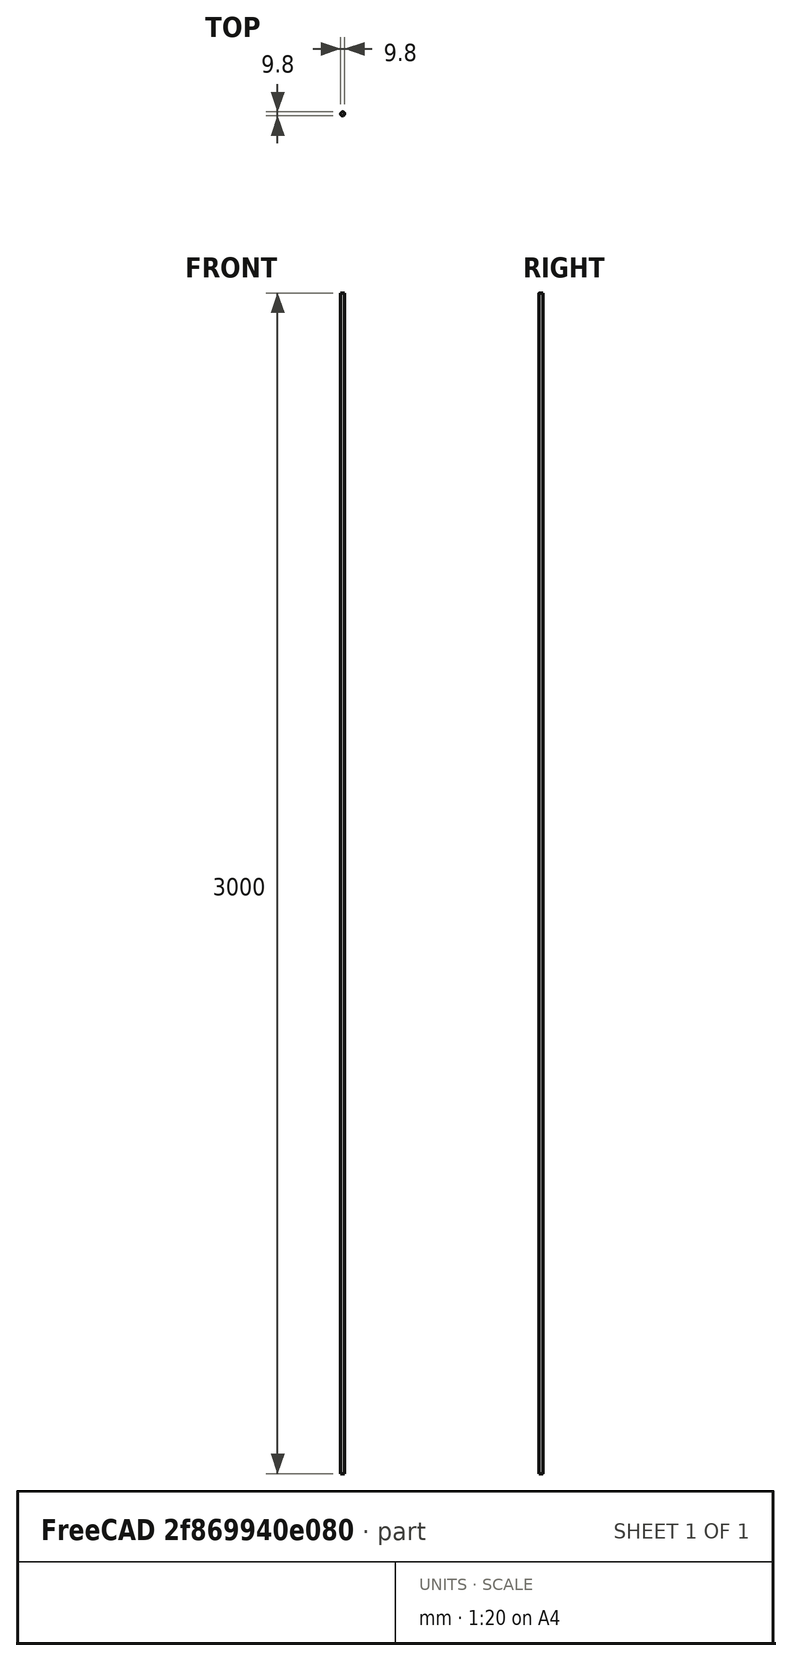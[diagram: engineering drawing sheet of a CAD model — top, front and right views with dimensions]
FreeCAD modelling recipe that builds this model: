
FCSTD DOCUMENT  (FreeCAD 0.21R33771 (Git))
Label: longFuelLowRes
License: All rights reserved
LicenseURL: http://en.wikipedia.org/wiki/All_rights_reserved
objects: Part::FeaturePython×5, App::DocumentObjectGroupPython×2, Sketcher::SketchObject×1, PartDesign::Pad×1, PartDesign::Body×1, App::MaterialObjectPython×1, Fem::FemMeshObject×1
note: 9 computed .brp shape members not serialized (recipe doc carries the construction recipe); baked Part::Feature solids carry a one-line shape summary decoded from their .brp

FEATURE [Sketcher::SketchObject] Sketch
  FullyConstrained = true
  MapMode = 5
  Support = -> [XY_Plane]
  sketch-geometry (1):
    g0: Circle CenterX=0 CenterY=0 CenterZ=0 NormalX=0 NormalY=0 NormalZ=1 AngleXU=0 Radius=4.9
  constraints (2):
    c: Coincident(g0,g-1)
    c: Diameter(g0) = 9.8
FEATURE [PartDesign::Pad] Pad
  Direction = (0,0,1)
  Length = 3000
  Length2 = 10
  Profile = -> Sketch
  ReferenceAxis = -> Sketch [N_Axis]
  Type = 0
FEATURE [PartDesign::Body] Body
  Group = -> [Sketch,Pad]
  Origin = -> Origin
  Tip = -> Pad
FEATURE [Part::FeaturePython] PhysicsModel  # WARN: FeaturePython — macro-defined, semantics opaque (R4)
  Flow = 1
  Phase = 0
  SRFModelAxis = (0,0,0)
  SRFModelCoR = (0,0,0)
  SRFModelEnabled = false
  SRFModelRPM = 0
  Time = 0
  Turbulence = 1
  TurbulenceModel = 0
  gx = 0
  gy = 0
  gz = -9800
FEATURE [App::MaterialObjectPython] FluidProperties  label="Air"  # material (typed FeaturePython)
  Category = 1
  Material = CardName=AirCompressible; Cp=1004.703 J/kg/K; Description=Compressible air properties; MolarMass=0.0289643897748887 kg/mol; Name=Air; SutherlandRefTemperature=273.15 K; SutherlandRefViscosity=1.716e-5 kg/m/s; SutherlandTemperature=110.4 K; Type=Compressible
FEATURE [Part::FeaturePython] InitialiseFields  # WARN: FeaturePython — macro-defined, semantics opaque (R4)
  PotentialFlow = false
  PotentialFlowP = false
  Pressure = 100
  ReThetat = 1
  Temperature = 800
  UseInletTemperatureValue = false
  UseInletTurbulenceValues = false
  UseInletUValues = false
  UseOutletPValue = false
  Ux = 0
  Uy = 0
  Uz = 0
  epsilon = 50000000
  gammaInt = 1
  k = 10000
  nuTilda = 55000000
  nut = 50000000
  omega = 1
FEATURE [Part::FeaturePython] CfdSolver  # WARN: FeaturePython — macro-defined, semantics opaque (R4)
  ConvergenceTol = 0.001
  EndTime = 1
  InputCaseName = case
  MaxCFLNumber = 5
  MaxInterfaceCFLNumber = 5
  MaxIterations = 2000
  Parallel = true
  ParallelCores = 4
  PurgeWrite = 0
  StartFrom = 0
  SteadyWriteInterval = 100
  TimeStep = 0.001
  TransientWriteInterval = 0.1
FEATURE [Part::FeaturePython] CfdFluidBoundary001  label="endCaps"  # WARN: FeaturePython — macro-defined, semantics opaque (R4)
  BoundarySubType = 0
  BoundaryType = 0
  DefaultBoundary = false
  DissipationRate = 50000000
  HeatFlux = 0
  HeatTransferCoeff = 0
  Intermittency = 1
  MassFlowRate = 0
  NuTilda = 55000000
  PeriodicCentreOfRotation = (0,0,0)
  PeriodicCentreOfRotationAxis = (0,0,0)
  PeriodicMaster = true
  PeriodicSeparationVector = (0,0,0)
  PorousBaffleMethod = 0
  Pressure = 100
  PressureDropCoeff = 0
  ReThetat = 1
  RelativeToFrame = false
  ReverseNormal = false
  RotationalPeriodic = false
  RoughnessConstant = 0.5
  RoughnessHeight = 0
  ScreenSpacing = 2
  ScreenWireDiameter = 0.2
  ShapeRefs = -> [Pad]
  SlipRatio = 0
  SpecificDissipationRate = 1
  Temperature = 290
  ThermalBoundaryType = 1
  TurbulenceInletSpecification = 6
  TurbulenceIntensityPercentage = 1
  TurbulenceLengthScale = 100
  TurbulentKineticEnergy = 10000
  TurbulentViscosity = 50000000
  Ux = 0
  Uy = 0
  Uz = 0
  VelocityIsCartesian = true
  VelocityMag = 0
  VolFlowRate = 0
  kEqnTurbulentKineticEnergy = 10000
  kEqnTurbulentViscosity = 50000000
FEATURE [Part::FeaturePython] CfdFluidBoundary  label="circularWall"  # WARN: FeaturePython — macro-defined, semantics opaque (R4)
  BoundarySubType = 0
  BoundaryType = 0
  DefaultBoundary = false
  DissipationRate = 50000000
  HeatFlux = 220000
  HeatTransferCoeff = 0
  Intermittency = 1
  MassFlowRate = 0
  NuTilda = 55000000
  PeriodicCentreOfRotation = (0,0,0)
  PeriodicCentreOfRotationAxis = (0,0,0)
  PeriodicMaster = true
  PeriodicSeparationVector = (0,0,0)
  PorousBaffleMethod = 0
  Pressure = 100
  PressureDropCoeff = 0
  ReThetat = 1
  RelativeToFrame = false
  ReverseNormal = false
  RotationalPeriodic = false
  RoughnessConstant = 0.5
  RoughnessHeight = 0
  ScreenSpacing = 2
  ScreenWireDiameter = 0.2
  ShapeRefs = -> [Pad]
  SlipRatio = 0
  SpecificDissipationRate = 1
  Temperature = 290
  ThermalBoundaryType = 2
  TurbulenceInletSpecification = 6
  TurbulenceIntensityPercentage = 1
  TurbulenceLengthScale = 100
  TurbulentKineticEnergy = 10000
  TurbulentViscosity = 50000000
  Ux = 0
  Uy = 0
  Uz = 0
  VelocityIsCartesian = true
  VelocityMag = 0
  VolFlowRate = 0
  kEqnTurbulentKineticEnergy = 10000
  kEqnTurbulentViscosity = 50000000
FEATURE [Fem::FemMeshObject] Pad_MeshSurfaceMesh
FEATURE [App::DocumentObjectGroupPython] Pad_Mesh  # scripted group (container) (typed FeaturePython)
  CaseName = meshCase
  CellsBetweenLevels = 3
  CharacteristicLengthMax = 0.8
  ConvertToDualMesh = false
  EdgeRefinement = 1
  ElementDimension = 1
  Group = -> [Pad_MeshSurfaceMesh]
  ImplicitEdgeDetection = false
  MeshUtility = 2
  NumberOfProcesses = 1
  NumberOfThreads = 0
  Part = -> Pad
  PointInMesh = x=0 m; y=0 m; z=0 m
  STLAngularMeshDensity = 100
  STLRelativeLinearDeflection = 0.001
FEATURE [App::DocumentObjectGroupPython] CfdAnalysis  # scripted group (container) (typed FeaturePython)
  Group = -> [PhysicsModel,FluidProperties,InitialiseFields,CfdSolver,CfdFluidBoundary001,CfdFluidBoundary,Pad_Mesh]
  HostfileName = ../mpi_hostfile
  IsActiveAnalysis = true
  NeedsCaseRewrite = false
  NeedsMeshRerun = false
  NeedsMeshRewrite = false
  UseHostfile = false
